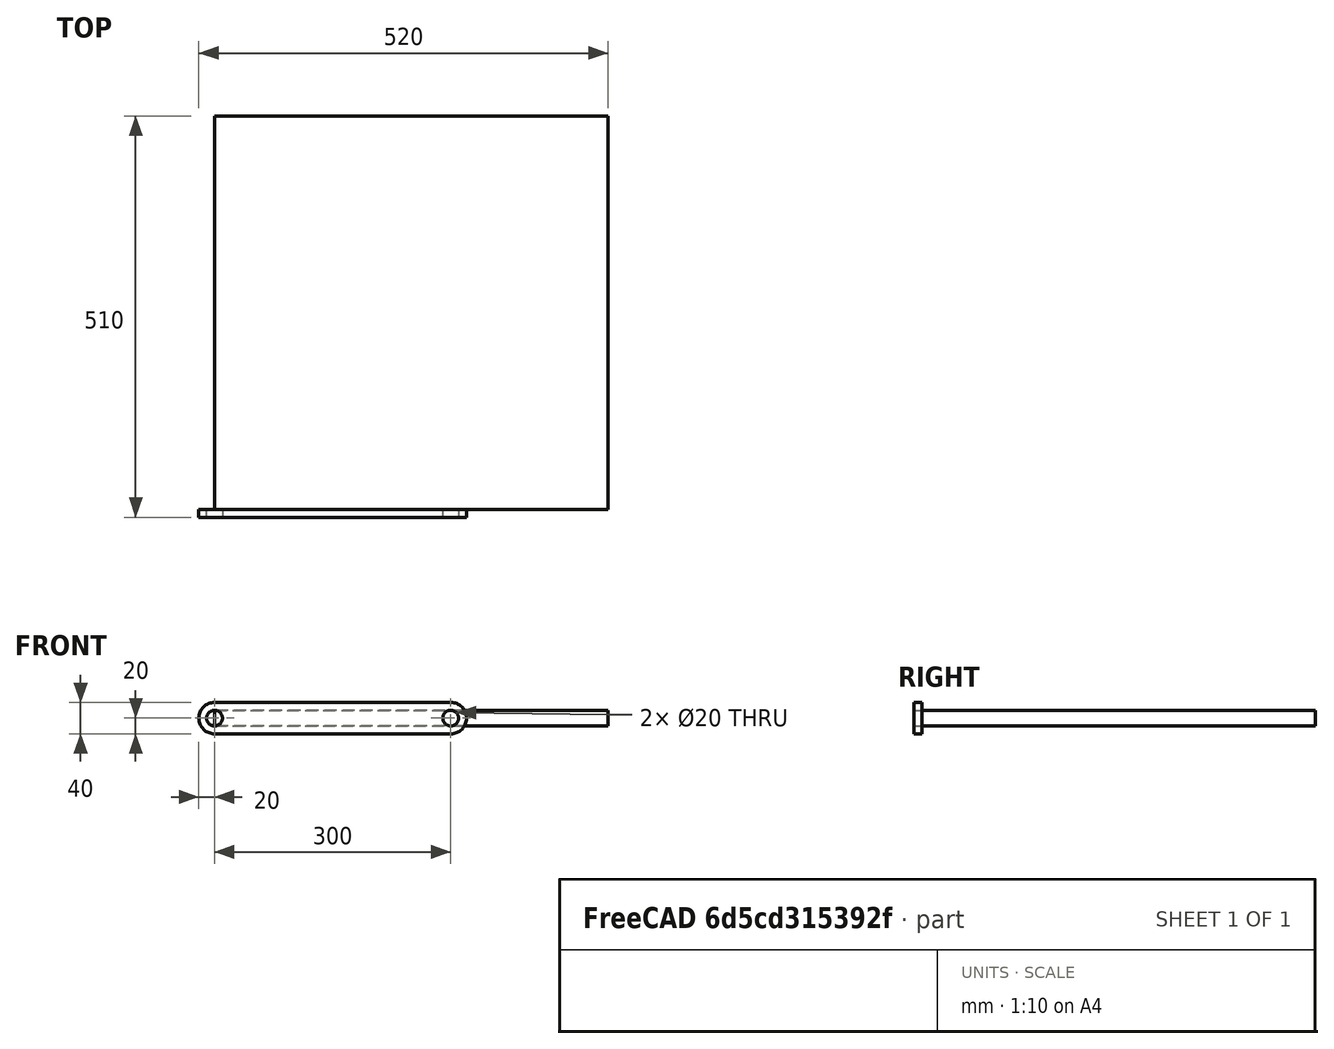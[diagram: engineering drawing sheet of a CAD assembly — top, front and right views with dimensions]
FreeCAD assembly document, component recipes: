
FREECAD ASSEMBLY — COMPONENT RECIPES ("Assembly4Decouverte")

This assembly document has 3 components, labeled P0..P2 below (a component is one placed body or linked part). 2 of them carry a construction recipe — the FreeCAD feature program that regenerates the part from scratch, quoted from this document or its linked companion documents; the rest are supplied as boundary geometry only. No exploded tour is included for this assembly.
COMPONENT P0 — geometry summary ("Model"; no construction recipe available for this part):
  bounding box: 520.0 x 493.9 x 349.7 mm
  tessellated surface: 6,828 triangles
  volume: 8525322 mm^3 (9% of its bounding box)
COMPONENT P1 — recipe-attached ("Part", modeled in this document).
Construction recipe (the document's own serialized feature program — sketch geometry with constraints, then the solid features built on it; lengths are millimeters unless a unit is written):

FEATURE [PartDesign::CoordinateSystem] LCS_0001
  AttacherType = Attacher::AttachEngine3D
  MapMode = 2
  Support = -> [X_Axis002]
FEATURE [Sketcher::SketchObject] Sketch
  FullyConstrained = true
  MapMode = 5
  Placement = pos=(0,0,0) rot=(1,0,0;1.5708rad)
  Support = -> [XZ_Plane002]
  expr: Constraints[12] = Sketch_1.Constraints.lg_bielle2
  sketch-geometry (6):
    g0: ArcOfCircle CenterX=0 CenterY=0 CenterZ=0 NormalX=0 NormalY=0 NormalZ=1 AngleXU=0 Radius=20 StartAngle=1.5708 EndAngle=4.71239
    g1: ArcOfCircle CenterX=300 CenterY=5e-16 CenterZ=0 NormalX=0 NormalY=0 NormalZ=1 AngleXU=0 Radius=20 StartAngle=4.71239 EndAngle=7.85398
    g2: LineSegment StartX=-3.7e-15 StartY=-20 StartZ=0 EndX=300 EndY=-20 EndZ=0
    g3: LineSegment StartX=-3.2e-15 StartY=20 StartZ=0 EndX=300 EndY=20 EndZ=0
    g4: Circle CenterX=0 CenterY=0 CenterZ=0 NormalX=0 NormalY=0 NormalZ=1 AngleXU=0 Radius=10
    g5: Circle CenterX=300 CenterY=5e-16 CenterZ=0 NormalX=0 NormalY=0 NormalZ=1 AngleXU=0 Radius=10
  constraints (13):
    c: Tangent(g0,g3) = 1.5708
    c: Tangent(g0,g2) = -1.5708
    c: Tangent(g2,g1) = -1.5708
    c: Tangent(g3,g1) = 1.5708
    c: Horizontal(g2)
    c: Equal(g0,g1)
    c: Coincident(g0,g-1)
    c: Coincident(g4,g0)
    c: Coincident(g5,g1)
    c: Equal(g4,g5)
    c: Radius(g0) = 20
    c: Radius(g4) = 10
    c: DistanceX(g0,g1) = 300
FEATURE [PartDesign::Pad] Pad
  Direction = (1,1,1)
  Length = 10
  Length2 = 100
  Placement = pos=(0,0,0) rot=(1,0,0;1.5708rad)
  Profile = -> Sketch
  Refine = true
  Type = 0
FEATURE [PartDesign::Body] Body
  Group = -> [LCS_0001,Sketch,Pad]
  Origin = -> Origin002
  Tip = -> Pad
COMPONENT P2 — recipe-attached ("Part_facade", modeled in this document).
Construction recipe (the document's own serialized feature program — sketch geometry with constraints, then the solid features built on it; lengths are millimeters unless a unit is written):

FEATURE [PartDesign::CoordinateSystem] LCS_0003
  AttacherType = Attacher::AttachEngine3D
  MapMode = 2
  Support = -> [X_Axis004]
FEATURE [Sketcher::SketchObject] Sketch001
  FullyConstrained = true
  MapMode = 5
  Support = -> [XY_Plane004]
  expr: Constraints[9] = Sketch_1.Constraints.hauteur_facade
  sketch-geometry (4):
    g0: LineSegment StartX=0 StartY=0 StartZ=0 EndX=500 EndY=0 EndZ=0
    g1: LineSegment StartX=500 StartY=0 StartZ=0 EndX=500 EndY=500 EndZ=0
    g2: LineSegment StartX=500 StartY=500 StartZ=0 EndX=0 EndY=500 EndZ=0
    g3: LineSegment StartX=0 StartY=500 StartZ=0 EndX=0 EndY=0 EndZ=0
  constraints (12):
    c: Coincident(g0,g1)
    c: Coincident(g1,g2)
    c: Coincident(g2,g3)
    c: Coincident(g3,g0)
    c: Horizontal(g0)
    c: Horizontal(g2)
    c: Vertical(g1)
    c: Vertical(g3)
    c: DistanceX(g2,g2) = 500  'largeur_facade'
    c: DistanceY(g3,g3) = 500
    c: DistanceX(g0) = 0
    c: DistanceY(g0) = 0
FEATURE [PartDesign::Pad] Pad001
  Direction = (1,1,1)
  Length = 20
  Length2 = 100
  Midplane = true
  Profile = -> Sketch001
  Refine = true
  Type = 0
FEATURE [PartDesign::Body] Body_facade
  Group = -> [LCS_0003,Sketch001,Pad001]
  Origin = -> Origin004
  Tip = -> Pad001
PROVENANCE & LICENSES
A FreeCAD (.FCStd) document from a public repository crawl; recipes are the document's own serialized feature recipes (and, for linked parts, companion documents' recipes).
License: cc0-1.0.
